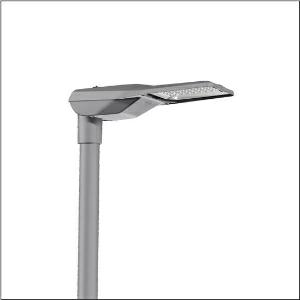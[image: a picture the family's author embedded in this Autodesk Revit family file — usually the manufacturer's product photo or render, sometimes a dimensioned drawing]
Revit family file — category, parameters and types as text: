
# Revit family: streetlight_sl_21_iq_mini___st1_0ab_5xe2m31v08gb_27e0
name_source: partatom
category: Lighting Fixtures
units: mm (PartAtom-declared; Revit-internal decimal feet)

## family parameters
Cut with Voids When Loaded = No
Host = Face
Light Source = No
Part Type = Normal
Room Calculation Point = No
Round Connector Dimension = Use Diameter
Shared = No

## types (1)
- --- (1 x LED, 5270 lm, 39.8 W, 3000K)
    Apparent Load = 40 VA
    CIE Flux Codes = 38 73 97 100 100
    Color Rendering = 70
    Color Temperature = 3000K
    Default Elevation = 1800 mm
    Description = Streetlight SL 21 iQ mini, mast luminaire, primary light control with lens, of PMMA, primary optical cover: cover, of toughened safety glass, transparent, light distribution: ST1.0aB, light emission: direct distribution, primary light characteristic: asymmetric, installation type: post-top, side-entry, LED, High Power LED, rated luminous flux: 5.270lm, luminous efficacy: 132lm/W, light colour: 730, colour temperature: 3000K, control: presetting dimming logarithmic, Street-Remote, Auto-Match, Temp-Guard, Lumen-Switch, Night-Set, Smart-Wire, Light-Fading, Desk-Remote (wireless, voltage-free reading and setting of iQ features in the workshop via application-optimized NFC function/RFID function), optimised constant luminous flux control (CLO 2.0), mains connection: 220..240V, AC, 50/60Hz, start of lifetime: 40W, end of service life: 41W, reduction: 18W, luminaire housing, of diecast aluminium, powder-coated, Siteco® metallic grey (DB 702S), corrosivity category C5 mid according to DIN EN ISO 12944, please order mast flange separately, inclination adjustable: 0°, 5°, 10°, 15°, sealing non-destructively replaceable, multi-level sealing system, length: 628mm, width: 235mm, height: 110mm, mast flange for spigot size: 42mm (side-entry): 5XC10008XM4, 60/48mm (side-entry/post-top): 5XC10108XM2, 76/60mm (side-entry/post-top): 5XC10108XM1, Smart Interface above, protection rating (complete): IP66, insulation class (complete): insulation class II (safety insulation), certification: CE, ENEC, ENEC+, VDE, impact resistance: IK09, permissible operating ambient temperature for outdoor applications: -40..+50°C, standard-compliant lighting for roads and squares, packaging unit: 1 piece

Light Distribution: ST1.0aB
    Height = 110 mm
    Lamp = 1 x LED
    Lamp Light Flux = 5270 lm
    Lamp Power = 39.8 W
    Lamp count = 1
    Length = 625 mm
    Luminous efficacy = 132 lm/W
    Manufacturer = Siteco
    ModVariant = No
    Model = 5XE2M31V08GB
    Number of Poles = 1
    OnlyDefault = Yes
    Power Factor = 1
    Product Name = Streetlight SL 21 iQ mini | ST1.0aB
    Product group = mast luminaire | pylon top
    ProductGroupID = 6100
    Protection Class = Protection class II
    Protection Degree = IP 66
    RLX_Detail_Level = 1
    RLX_Emergency_Light_Flux = 0 lm
    RLX_Emergency_Type = 0
    RLX_Emergency_Type_DB = No
    RlxData = <blob elided: 94189 chars, md5=f2fbc5f0>
    Socket = socket
    Standby Power = 0 W
    System Light Flux = 5270 lm
    System Power = 40 W
    Type Comments = factory setting: luminous flux: 100 % | dim-lin: 254 | 800 mA
    Type Image = l_1003515.jpg
    URL = http://relux.com
    VarID = @adj_042599
    Voltage = 0 V
    Weight = 0.00 kg
    Width = 234 mm

## geometry (parser evidence)
native form markers: Blend x4, Sweep x10
no freeform markers — native parametric forms only
